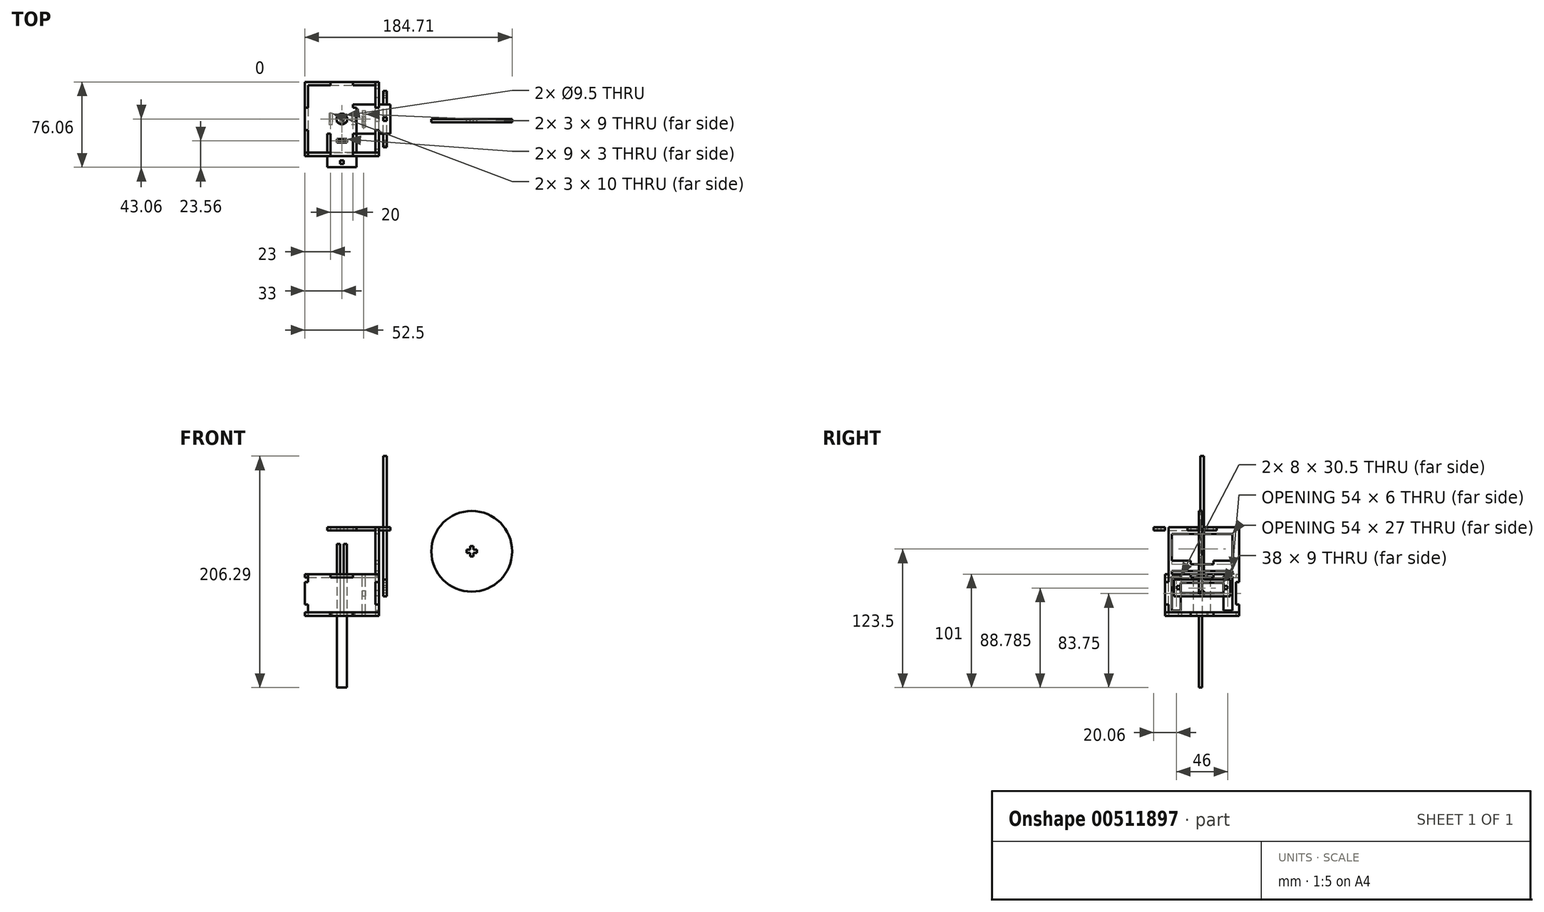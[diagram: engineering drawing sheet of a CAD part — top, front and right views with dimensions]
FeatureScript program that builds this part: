
annotation { "Feature Type Name" : "Feature", "Feature Type Description" : "" }
export const myFeature = defineFeature(function(context is Context, id is Id, definition is map)
    precondition{}
    {
        {
            var Q0;
            Q0=qCreatedBy(makeId("Top.planeOp"),FACE);
            var sketch = newSketch(context, id + "F0", { "sketchPlane" : qUnion([Q0])});
            skLineSegment(sketch, "E0.bottom", {"start": v(33, 33) * mm, "end": v(-33, 33) * mm});
            skLineSegment(sketch, "E0.top", {"start": v(33, -33) * mm, "end": v(-33, -33) * mm});
            skLineSegment(sketch, "E0.left", {"start": v(33, 33) * mm, "end": v(33, -33) * mm});
            skLineSegment(sketch, "E0.right", {"start": v(-33, 33) * mm, "end": v(-33, -33) * mm});
            skLineSegment(sketch, "E1.bottom", {"start": v(-10, 33) * mm, "end": v(10, 33) * mm});
            skLineSegment(sketch, "E1.top", {"start": v(-10, 30) * mm, "end": v(10, 30) * mm});
            skLineSegment(sketch, "E1.left", {"start": v(-10, 33) * mm, "end": v(-10, 30) * mm});
            skLineSegment(sketch, "E1.right", {"start": v(10, 33) * mm, "end": v(10, 30) * mm});
            skLineSegment(sketch, "E2.bottom", {"start": v(33, 10) * mm, "end": v(30, 10) * mm});
            skLineSegment(sketch, "E2.top", {"start": v(33, -10) * mm, "end": v(30, -10) * mm});
            skLineSegment(sketch, "E2.left", {"start": v(33, 10) * mm, "end": v(33, -10) * mm});
            skLineSegment(sketch, "E2.right", {"start": v(30, 10) * mm, "end": v(30, -10) * mm});
            skLineSegment(sketch, "E3.bottom", {"start": v(10, -33) * mm, "end": v(-10, -33) * mm});
            skLineSegment(sketch, "E3.top", {"start": v(10, -30) * mm, "end": v(-10, -30) * mm});
            skLineSegment(sketch, "E3.left", {"start": v(10, -33) * mm, "end": v(10, -30) * mm});
            skLineSegment(sketch, "E3.right", {"start": v(-10, -33) * mm, "end": v(-10, -30) * mm});
            skLineSegment(sketch, "E4.bottom", {"start": v(-33, 10) * mm, "end": v(-30, 10) * mm});
            skLineSegment(sketch, "E4.top", {"start": v(-33, -10) * mm, "end": v(-30, -10) * mm});
            skLineSegment(sketch, "E4.left", {"start": v(-33, 10) * mm, "end": v(-33, -10) * mm});
            skLineSegment(sketch, "E4.right", {"start": v(-30, 10) * mm, "end": v(-30, -10) * mm});
            skPoint(sketch, "E5", {"position": v(-30, 0) * mm});
            skPoint(sketch, "E6", {"position": v(0, 30) * mm});
            skPoint(sketch, "E7", {"position": v(0, -30) * mm});
            skPoint(sketch, "E8", {"position": v(30, 0) * mm});
            skCircle(sketch, "E9", {"center": v(0, 0) * mm, "radius": 4.75 * mm});
            skLineSegment(sketch, "E10.bottom", {"start": v(-8.5, 5) * mm, "end": v(-11.5, 5) * mm});
            skLineSegment(sketch, "E10.top", {"start": v(-8.5, -5) * mm, "end": v(-11.5, -5) * mm});
            skLineSegment(sketch, "E10.left", {"start": v(-8.5, 5) * mm, "end": v(-8.5, -5) * mm});
            skLineSegment(sketch, "E10.right", {"start": v(-11.5, 5) * mm, "end": v(-11.5, -5) * mm});
            skPoint(sketch, "E10.middle", {"position": v(-10, 0) * mm});
            skLineSegment(sketch, "E11.bottom", {"start": v(11.5, 5) * mm, "end": v(8.5, 5) * mm});
            skLineSegment(sketch, "E11.top", {"start": v(11.5, -5) * mm, "end": v(8.5, -5) * mm});
            skLineSegment(sketch, "E11.left", {"start": v(11.5, 5) * mm, "end": v(11.5, -5) * mm});
            skLineSegment(sketch, "E11.right", {"start": v(8.5, 5) * mm, "end": v(8.5, -5) * mm});
            skPoint(sketch, "E11.middle", {"position": v(10, 0) * mm});
            skLineSegment(sketch, "E12", {"start": v(33, 0) * mm, "end": v(-33, 0) * mm, "construction": true});
            skSolve(sketch);
        }
        {
            var Q0;
            Q0=makeQuery(id+"F0.imprint","IMPRINT",FACE,{"disambiguationData":[TD([[makeQuery(id+"F0.imprint","IMPRINT",EDGE,{"derivedFrom":sQuery(id+"F0.wireOp",EDGE,"E0.bottom")}),1.0]])]});
            extrude(context, id + "F1", {"entities" : qUnion([Q0]), "depth" : 3 * mm, "offsetDistance" : 25 * mm});
        }
        {
            var Q0;
            Q0=makeQuery(id+"F1.opExtrude","SWEPT_FACE",FACE,{"disambiguationData":[OSD([sQuery(id+"F0.wireOp",EDGE,"E2.right")])]});
            var sketch = newSketch(context, id + "F2", { "sketchPlane" : qUnion([Q0])});
            skLineSegment(sketch, "E13.bottom", {"start": v(-33, 3) * mm, "end": v(33, 3) * mm});
            skLineSegment(sketch, "E13.top", {"start": v(-33, 37) * mm, "end": v(33, 37) * mm});
            skLineSegment(sketch, "E13.left", {"start": v(-33, 3) * mm, "end": v(-33, 37) * mm});
            skLineSegment(sketch, "E13.right", {"start": v(33, 3) * mm, "end": v(33, 37) * mm});
            skLineSegment(sketch, "E14.bottom", {"start": v(-10, 3) * mm, "end": v(10, 3) * mm});
            skLineSegment(sketch, "E14.top", {"start": v(-10, 0) * mm, "end": v(10, 0) * mm});
            skLineSegment(sketch, "E14.left", {"start": v(-10, 3) * mm, "end": v(-10, 0) * mm});
            skLineSegment(sketch, "E14.right", {"start": v(10, 3) * mm, "end": v(10, 0) * mm});
            skCircle(sketch, "E15", {"center": v(0, 20) * mm, "radius": 2.3 * mm});
            skLineSegment(sketch, "E16.bottom", {"start": v(33, 30) * mm, "end": v(30, 30) * mm});
            skLineSegment(sketch, "E16.top", {"start": v(33, 10) * mm, "end": v(30, 10) * mm});
            skLineSegment(sketch, "E16.left", {"start": v(33, 30) * mm, "end": v(33, 10) * mm});
            skLineSegment(sketch, "E16.right", {"start": v(30, 30) * mm, "end": v(30, 10) * mm});
            skLineSegment(sketch, "E17.bottom", {"start": v(-33, 30) * mm, "end": v(-30, 30) * mm});
            skLineSegment(sketch, "E17.top", {"start": v(-33, 10) * mm, "end": v(-30, 10) * mm});
            skLineSegment(sketch, "E17.left", {"start": v(-33, 30) * mm, "end": v(-33, 10) * mm});
            skLineSegment(sketch, "E17.right", {"start": v(-30, 30) * mm, "end": v(-30, 10) * mm});
            skLineSegment(sketch, "E18.bottom", {"start": v(10, 37) * mm, "end": v(-10, 37) * mm});
            skLineSegment(sketch, "E18.top", {"start": v(10, 34) * mm, "end": v(-10, 34) * mm});
            skLineSegment(sketch, "E18.left", {"start": v(10, 37) * mm, "end": v(10, 34) * mm});
            skLineSegment(sketch, "E18.right", {"start": v(-10, 37) * mm, "end": v(-10, 34) * mm});
            skPoint(sketch, "E19", {"position": v(0, 34) * mm});
            skPoint(sketch, "E20", {"position": v(30, 20) * mm});
            skPoint(sketch, "E21", {"position": v(-30, 20) * mm});
            skLineSegment(sketch, "E22", {"start": v(-33, 37) * mm, "end": v(-33, 49) * mm});
            skLineSegment(sketch, "E23", {"start": v(-33, 49) * mm, "end": v(-10, 49) * mm});
            skLineSegment(sketch, "E24", {"start": v(-10, 49) * mm, "end": v(-10, 46) * mm});
            skLineSegment(sketch, "E25", {"start": v(-10, 46) * mm, "end": v(10, 46) * mm});
            skLineSegment(sketch, "E26", {"start": v(10, 46) * mm, "end": v(10, 49) * mm});
            skLineSegment(sketch, "E27", {"start": v(10, 49) * mm, "end": v(33, 49) * mm});
            skLineSegment(sketch, "E28", {"start": v(33, 49) * mm, "end": v(33, 37) * mm});
            skLineSegment(sketch, "E29", {"start": v(0, 20) * mm, "end": v(0, 46) * mm, "construction": true});
            skLineSegment(sketch, "E30", {"start": v(-27, 37) * mm, "end": v(-27, 40) * mm});
            skLineSegment(sketch, "E31", {"start": v(-27, 40) * mm, "end": v(27, 40) * mm});
            skLineSegment(sketch, "E32", {"start": v(27, 40) * mm, "end": v(27, 37) * mm});
            skPoint(sketch, "E33", {"position": v(0, 40) * mm});
            skLineSegment(sketch, "E34", {"start": v(-33, 49) * mm, "end": v(-33, 79) * mm});
            skLineSegment(sketch, "E35", {"start": v(-33, 79) * mm, "end": v(-10, 79) * mm});
            skLineSegment(sketch, "E36", {"start": v(-10, 79) * mm, "end": v(-10, 76) * mm});
            skLineSegment(sketch, "E37", {"start": v(-10, 76) * mm, "end": v(10, 76) * mm});
            skLineSegment(sketch, "E38", {"start": v(10, 76) * mm, "end": v(10, 79) * mm});
            skLineSegment(sketch, "E39", {"start": v(10, 79) * mm, "end": v(33, 79) * mm});
            skLineSegment(sketch, "E40", {"start": v(33, 79) * mm, "end": v(33, 49) * mm});
            skLineSegment(sketch, "E41", {"start": v(-27, 49) * mm, "end": v(-27, 73) * mm});
            skLineSegment(sketch, "E42", {"start": v(-27, 73) * mm, "end": v(27, 73) * mm});
            skLineSegment(sketch, "E43", {"start": v(27, 73) * mm, "end": v(27, 49) * mm});
            skPoint(sketch, "E44", {"position": v(0, 73) * mm});
            skLineSegment(sketch, "E45", {"start": v(0, 46) * mm, "end": v(0, 73) * mm, "construction": true});
            skLineSegment(sketch, "E46", {"start": v(-30, 30) * mm, "end": v(-30, 37) * mm});
            skLineSegment(sketch, "E47", {"start": v(-30, 10) * mm, "end": v(-30, 3) * mm});
            skLineSegment(sketch, "E48", {"start": v(-30, 37) * mm, "end": v(-30, 79) * mm});
            skLineSegment(sketch, "E49.bottom", {"start": v(-27, 37) * mm, "end": v(-24, 37) * mm});
            skLineSegment(sketch, "E50.bottom", {"start": v(27, 37) * mm, "end": v(24, 37) * mm});
            skLineSegment(sketch, "E51.bottom", {"start": v(27, 3) * mm, "end": v(24, 3) * mm});
            skLineSegment(sketch, "E52.bottom", {"start": v(-27, 35) * mm, "end": v(-19, 35) * mm});
            skLineSegment(sketch, "E52.top", {"start": v(-27, 4.5) * mm, "end": v(-19, 4.5) * mm});
            skLineSegment(sketch, "E52.left", {"start": v(-27, 35) * mm, "end": v(-27, 4.5) * mm});
            skLineSegment(sketch, "E52.right", {"start": v(-19, 35) * mm, "end": v(-19, 4.5) * mm});
            skLineSegment(sketch, "E53.bottom", {"start": v(27, 35) * mm, "end": v(19, 35) * mm});
            skLineSegment(sketch, "E53.top", {"start": v(27, 4.5) * mm, "end": v(19, 4.5) * mm});
            skLineSegment(sketch, "E53.left", {"start": v(27, 35) * mm, "end": v(27, 4.5) * mm});
            skLineSegment(sketch, "E53.right", {"start": v(19, 35) * mm, "end": v(19, 4.5) * mm});
            skSolve(sketch);
        }
        {
            var Q0;
            Q0=makeQuery(id+"F2.imprint","IMPRINT",FACE,{"disambiguationData":[TD([[makeQuery(id+"F2.imprint","IMPRINT",EDGE,{"derivedFrom":sQuery(id+"F2.wireOp",EDGE,"E13.top")}),-1.0]])]});
            var Q1;
            Q1=makeQuery(id+"F2.imprint","IMPRINT",FACE,{"disambiguationData":[TD([[makeQuery(id+"F2.imprint","IMPRINT",EDGE,{"derivedFrom":sQuery(id+"F2.wireOp",EDGE,"E14.bottom")}),1.0]])]});
            var Q2;
            Q2=makeQuery(id+"F2.imprint","IMPRINT",FACE,{"disambiguationData":[TD([[makeQuery(id+"F2.imprint","IMPRINT",EDGE,{"derivedFrom":sQuery(id+"F2.wireOp",EDGE,"E17.bottom")}),-1.0]])]});
            var Q3;
            {var subQ7=sQuery(id+"F2.wireOp",EDGE,"E36");Q3=makeQuery(id+"F2.imprint","IMPRINT",FACE,{"disambiguationData":[TD([[makeQuery(id+"F2.imprint","IMPRINT",EDGE,{"derivedFrom":subQ7}),-1.0]])]});}
            var Q4;
            {var subQ4=sQuery(id+"F2.wireOp",EDGE,"E24");Q4=makeQuery(id+"F2.imprint","IMPRINT",FACE,{"disambiguationData":[TD([[makeQuery(id+"F2.imprint","IMPRINT",EDGE,{"derivedFrom":subQ4}),-1.0]])]});}
            extrude(context, id + "F3", {"entities" : qUnion([Q0, Q1, Q2, Q3, Q4]), "depth" : 3 * mm, "offsetDistance" : 25 * mm});
        }
        {
            var Q0;
            Q0=qCreatedBy(makeId("Front.planeOp"),FACE);
            var sketch = newSketch(context, id + "F4", { "sketchPlane" : qUnion([Q0])});
            skLineSegment(sketch, "E54.bottom", {"start": v(4.5, 64) * mm, "end": v(-4.5, 64) * mm});
            skLineSegment(sketch, "E54.top", {"start": v(4.5, -64) * mm, "end": v(-4.5, -64) * mm});
            skLineSegment(sketch, "E54.left", {"start": v(4.5, 64) * mm, "end": v(4.5, -64) * mm});
            skLineSegment(sketch, "E54.right", {"start": v(-4.5, 64) * mm, "end": v(-4.5, -64) * mm});
            skPoint(sketch, "E54.middle", {"position": v(0, 0) * mm});
            skLineSegment(sketch, "E55.bottom", {"start": v(-1.5, 64) * mm, "end": v(1.5, 64) * mm});
            skLineSegment(sketch, "E55.top", {"start": v(-1.5, 0) * mm, "end": v(1.5, 0) * mm});
            skLineSegment(sketch, "E55.left", {"start": v(-1.5, 64) * mm, "end": v(-1.5, 0) * mm});
            skLineSegment(sketch, "E55.right", {"start": v(1.5, 64) * mm, "end": v(1.5, 0) * mm});
            skSolve(sketch);
        }
        {
            var Q0;
            Q0=makeQuery(id+"F4.imprint","IMPRINT",FACE,{"disambiguationData":[TD([[makeQuery(id+"F4.imprint","IMPRINT",EDGE,{"derivedFrom":sQuery(id+"F4.wireOp",EDGE,"E54.top")}),-1.0]])]});
            extrude(context, id + "F5", {"entities" : qUnion([Q0]), "depth" : 3 * mm, "offsetDistance" : 25 * mm});
        }
        {
            var Q0;
            Q0=makeQuery(id+"F3.opExtrude","SWEPT_FACE",FACE,{"disambiguationData":[OSD([sQuery(id+"F2.wireOp",EDGE,"E18.top")])]});
            var sketch = newSketch(context, id + "F6", { "sketchPlane" : qUnion([Q0])});
            skLineSegment(sketch, "E56.bottom", {"start": v(-30, -30) * mm, "end": v(30, -30) * mm});
            skLineSegment(sketch, "E56.top", {"start": v(-30, 30) * mm, "end": v(30, 30) * mm});
            skLineSegment(sketch, "E56.left", {"start": v(-30, -30) * mm, "end": v(-30, 30) * mm});
            skLineSegment(sketch, "E56.right", {"start": v(30, -30) * mm, "end": v(30, 30) * mm});
            skLineSegment(sketch, "E57.bottom", {"start": v(10, 30) * mm, "end": v(-10, 30) * mm});
            skLineSegment(sketch, "E57.top", {"start": v(10, 33) * mm, "end": v(-10, 33) * mm});
            skLineSegment(sketch, "E57.left", {"start": v(10, 30) * mm, "end": v(10, 33) * mm});
            skLineSegment(sketch, "E57.right", {"start": v(-10, 30) * mm, "end": v(-10, 33) * mm});
            skLineSegment(sketch, "E58.bottom", {"start": v(10, -30) * mm, "end": v(-10, -30) * mm});
            skLineSegment(sketch, "E58.top", {"start": v(10, -33) * mm, "end": v(-10, -33) * mm});
            skLineSegment(sketch, "E58.left", {"start": v(10, -30) * mm, "end": v(10, -33) * mm});
            skLineSegment(sketch, "E58.right", {"start": v(-10, -30) * mm, "end": v(-10, -33) * mm});
            skLineSegment(sketch, "E59.bottom", {"start": v(30, -10) * mm, "end": v(33, -10) * mm});
            skLineSegment(sketch, "E59.top", {"start": v(30, 10) * mm, "end": v(33, 10) * mm});
            skLineSegment(sketch, "E59.left", {"start": v(30, -10) * mm, "end": v(30, 10) * mm});
            skLineSegment(sketch, "E59.right", {"start": v(33, -10) * mm, "end": v(33, 10) * mm});
            skLineSegment(sketch, "E60.bottom", {"start": v(-30, 10) * mm, "end": v(-33, 10) * mm});
            skLineSegment(sketch, "E60.top", {"start": v(-30, -10) * mm, "end": v(-33, -10) * mm});
            skLineSegment(sketch, "E60.left", {"start": v(-30, 10) * mm, "end": v(-30, -10) * mm});
            skLineSegment(sketch, "E60.right", {"start": v(-33, 10) * mm, "end": v(-33, -10) * mm});
            skCircle(sketch, "E61", {"center": v(0, 0) * mm, "radius": 4.75 * mm});
            skSolve(sketch);
        }
        {
            var Q0;
            Q0 = qSketchRegion(id + "F6", true);
            extrude(context, id + "F7", {"entities" : qUnion([Q0]), "depth" : 3 * mm, "offsetDistance" : 25 * mm});
        }
        {
            var Q0;
            {var subQ0=sQuery(id+"F6.wireOp",EDGE,"E56.bottom");Q0=makeQuery(id+"F7.opExtrude","SWEPT_FACE",FACE,{"disambiguationData":[OSD([subQ0]),TDD([makeQuery(id+"F6.imprint","IMPRINT",EDGE,{"disambiguationData":[TD([[makeQuery(id+"F6.imprint","INTERSECT",VERTEX,{"derivedFrom":[subQ0,sQuery(id+"F6.wireOp",EDGE,"E56.right")]}),1.0]])],"derivedFrom":subQ0})])]});}
            var sketch = newSketch(context, id + "F8", { "sketchPlane" : qUnion([Q0])});
            skLineSegment(sketch, "E62.bottom", {"start": v(-30, 3) * mm, "end": v(30, 3) * mm});
            skLineSegment(sketch, "E62.top", {"start": v(-30, 37) * mm, "end": v(30, 37) * mm});
            skLineSegment(sketch, "E62.left", {"start": v(-30, 3) * mm, "end": v(-30, 37) * mm});
            skLineSegment(sketch, "E62.right", {"start": v(30, 3) * mm, "end": v(30, 37) * mm});
            skLineSegment(sketch, "E63.bottom", {"start": v(10, 37) * mm, "end": v(-10, 37) * mm});
            skLineSegment(sketch, "E63.top", {"start": v(10, 34) * mm, "end": v(-10, 34) * mm});
            skLineSegment(sketch, "E63.left", {"start": v(10, 34) * mm, "end": v(10, 37) * mm});
            skLineSegment(sketch, "E63.right", {"start": v(-10, 34) * mm, "end": v(-10, 37) * mm});
            skLineSegment(sketch, "E64.bottom", {"start": v(-30, 30) * mm, "end": v(-33, 30) * mm});
            skLineSegment(sketch, "E64.top", {"start": v(-30, 10) * mm, "end": v(-33, 10) * mm});
            skLineSegment(sketch, "E64.left", {"start": v(-30, 30) * mm, "end": v(-30, 10) * mm});
            skLineSegment(sketch, "E64.right", {"start": v(-33, 30) * mm, "end": v(-33, 10) * mm});
            skLineSegment(sketch, "E65.bottom", {"start": v(-10, 3) * mm, "end": v(10, 3) * mm});
            skLineSegment(sketch, "E65.top", {"start": v(-10, 0) * mm, "end": v(10, 0) * mm});
            skLineSegment(sketch, "E65.left", {"start": v(-10, 3) * mm, "end": v(-10, 0) * mm});
            skLineSegment(sketch, "E65.right", {"start": v(10, 3) * mm, "end": v(10, 0) * mm});
            skLineSegment(sketch, "E66.bottom", {"start": v(30, 10) * mm, "end": v(33, 10) * mm});
            skLineSegment(sketch, "E66.top", {"start": v(30, 30) * mm, "end": v(33, 30) * mm});
            skLineSegment(sketch, "E66.left", {"start": v(30, 10) * mm, "end": v(30, 30) * mm});
            skLineSegment(sketch, "E66.right", {"start": v(33, 10) * mm, "end": v(33, 30) * mm});
            skLineSegment(sketch, "E67.0", {"start": v(33, 37) * mm, "end": v(30, 37) * mm});
            skLineSegment(sketch, "E68.0", {"start": v(33, 30) * mm, "end": v(33, 37) * mm});
            skLineSegment(sketch, "E69.0", {"start": v(33, 10) * mm, "end": v(33, 3) * mm});
            skLineSegment(sketch, "E70.0", {"start": v(33, 3) * mm, "end": v(30, 3) * mm});
            skSolve(sketch);
        }
        {
            var Q0;
            Q0=makeQuery(id+"F8.imprint","IMPRINT",FACE,{"disambiguationData":[TD([[makeQuery(id+"F8.imprint","IMPRINT",EDGE,{"derivedFrom":sQuery(id+"F8.wireOp",EDGE,"E63.top")}),1.0]])]});
            var Q1;
            Q1=makeQuery(id+"F8.imprint","IMPRINT",FACE,{"disambiguationData":[TD([[makeQuery(id+"F8.imprint","IMPRINT",EDGE,{"derivedFrom":sQuery(id+"F8.wireOp",EDGE,"E64.bottom")}),1.0]])]});
            var Q2;
            Q2=makeQuery(id+"F8.imprint","IMPRINT",FACE,{"disambiguationData":[TD([[makeQuery(id+"F8.imprint","IMPRINT",EDGE,{"derivedFrom":sQuery(id+"F8.wireOp",EDGE,"E65.bottom")}),-1.0]])]});
            var Q3;
            Q3=makeQuery(id+"F8.imprint","IMPRINT",FACE,{"disambiguationData":[TD([[makeQuery(id+"F8.imprint","IMPRINT",EDGE,{"derivedFrom":sQuery(id+"F8.wireOp",EDGE,"E66.bottom")}),-1.0]])]});
            var Q4;
            {var subQ3=sQuery(id+"F8.wireOp",EDGE,"E63.left");Q4=makeQuery(id+"F8.imprint","IMPRINT",FACE,{"disambiguationData":[TD([[makeQuery(id+"F8.imprint","IMPRINT",EDGE,{"derivedFrom":subQ3}),1.0]])]});}
            var Q5;
            {var subQ4=sQuery(id+"F8.wireOp",EDGE,"E66.top");Q5=makeQuery(id+"F8.imprint","IMPRINT",FACE,{"disambiguationData":[TD([[makeQuery(id+"F8.imprint","IMPRINT",EDGE,{"derivedFrom":subQ4}),1.0]])]});}
            extrude(context, id + "F9", {"entities" : qUnion([Q0, Q1, Q2, Q3, Q4, Q5]), "depth" : 3 * mm, "offsetDistance" : 25 * mm});
        }
        {
            var Q0;
            Q0=makeQuery(id+"F3.opExtrude","SWEPT_FACE",FACE,{"disambiguationData":[OSD([sQuery(id+"F2.wireOp",EDGE,"E37")])]});
            var sketch = newSketch(context, id + "F10", { "sketchPlane" : qUnion([Q0])});
            skLineSegment(sketch, "E71.bottom", {"start": v(0, 10) * mm, "end": v(33, 10) * mm});
            skLineSegment(sketch, "E71.top", {"start": v(0, -10) * mm, "end": v(33, -10) * mm});
            skLineSegment(sketch, "E71.left", {"start": v(0, 10) * mm, "end": v(0, -10) * mm});
            skLineSegment(sketch, "E71.right", {"start": v(33, 10) * mm, "end": v(33, -10) * mm});
            skLineSegment(sketch, "E72.bottom", {"start": v(33, -13) * mm, "end": v(43.06, -13) * mm});
            skLineSegment(sketch, "E72.top", {"start": v(33, 13) * mm, "end": v(43.06, 13) * mm});
            skLineSegment(sketch, "E72.left", {"start": v(33, -13) * mm, "end": v(33, 13) * mm});
            skLineSegment(sketch, "E72.right", {"start": v(43.06, -13) * mm, "end": v(43.06, 13) * mm});
            skLineSegment(sketch, "E73", {"start": v(38.5, 13) * mm, "end": v(38.5, -13) * mm, "construction": true});
            skLineSegment(sketch, "E74.MirrorCS", {"start": v(-33, 10) * mm, "end": v(-33, -10) * mm});
            skLineSegment(sketch, "E75.MirrorCS", {"start": v(-33, -13) * mm, "end": v(-43.06, -13) * mm});
            skLineSegment(sketch, "E76.MirrorCS", {"start": v(-33, -13) * mm, "end": v(-33, 13) * mm});
            skLineSegment(sketch, "E77.MirrorCS", {"start": v(-43.06, -13) * mm, "end": v(-43.06, 13) * mm});
            skLineSegment(sketch, "E78.MirrorCS", {"start": v(-38.5, 13) * mm, "end": v(-38.5, -13) * mm, "construction": true});
            skLineSegment(sketch, "E79.MirrorCS", {"start": v(-33, 13) * mm, "end": v(-43.06, 13) * mm});
            skLineSegment(sketch, "E80.MirrorCS", {"start": v(0, -10) * mm, "end": v(-33, -10) * mm});
            skLineSegment(sketch, "E81.MirrorCS", {"start": v(0, 10) * mm, "end": v(-33, 10) * mm});
            skCircle(sketch, "E82", {"center": v(0, 0) * mm, "radius": 4.75 * mm});
            skLineSegment(sketch, "E83.bottom", {"start": v(40.06, 1.56) * mm, "end": v(36.94, 1.56) * mm});
            skLineSegment(sketch, "E83.top", {"start": v(40.06, -1.56) * mm, "end": v(36.94, -1.56) * mm});
            skLineSegment(sketch, "E83.left", {"start": v(40.06, 1.56) * mm, "end": v(40.06, -1.56) * mm});
            skLineSegment(sketch, "E83.right", {"start": v(36.94, 1.56) * mm, "end": v(36.94, -1.56) * mm});
            skPoint(sketch, "E83.middle", {"position": v(38.5, 0) * mm});
            skLineSegment(sketch, "E84.bottom", {"start": v(-36.94, 1.56) * mm, "end": v(-40.06, 1.56) * mm});
            skLineSegment(sketch, "E84.top", {"start": v(-36.94, -1.56) * mm, "end": v(-40.06, -1.56) * mm});
            skLineSegment(sketch, "E84.left", {"start": v(-36.94, 1.56) * mm, "end": v(-36.94, -1.56) * mm});
            skLineSegment(sketch, "E84.right", {"start": v(-40.06, 1.56) * mm, "end": v(-40.06, -1.56) * mm});
            skPoint(sketch, "E84.middle", {"position": v(-38.5, 0) * mm});
            skLineSegment(sketch, "E85.bottom", {"start": v(30, 10) * mm, "end": v(-30, 10) * mm});
            skLineSegment(sketch, "E85.top", {"start": v(30, 13) * mm, "end": v(-30, 13) * mm});
            skLineSegment(sketch, "E85.left", {"start": v(30, 10) * mm, "end": v(30, 13) * mm});
            skLineSegment(sketch, "E85.right", {"start": v(-30, 10) * mm, "end": v(-30, 13) * mm});
            skLineSegment(sketch, "E86.bottom", {"start": v(-30, -10) * mm, "end": v(30, -10) * mm});
            skLineSegment(sketch, "E86.top", {"start": v(-30, -13) * mm, "end": v(30, -13) * mm});
            skLineSegment(sketch, "E86.left", {"start": v(-30, -10) * mm, "end": v(-30, -13) * mm});
            skLineSegment(sketch, "E86.right", {"start": v(30, -10) * mm, "end": v(30, -13) * mm});
            skLineSegment(sketch, "E87.1.0", {"start": v(10, 0) * mm, "end": v(10, 33) * mm});
            skLineSegment(sketch, "E87.1.1", {"start": v(-13, 33) * mm, "end": v(13, 33) * mm});
            skLineSegment(sketch, "E87.1.2", {"start": v(13, -30) * mm, "end": v(13, 30) * mm});
            skLineSegment(sketch, "E87.1.3", {"start": v(10, -30) * mm, "end": v(10, 30) * mm});
            skLineSegment(sketch, "E87.1.4", {"start": v(13, 33) * mm, "end": v(13, 43.06) * mm});
            skPoint(sketch, "E87.1.5", {"position": v(0, -38.5) * mm});
            skLineSegment(sketch, "E87.1.6", {"start": v(-13, 43.06) * mm, "end": v(13, 43.06) * mm});
            skLineSegment(sketch, "E87.1.7", {"start": v(13, 38.5) * mm, "end": v(-13, 38.5) * mm, "construction": true});
            skLineSegment(sketch, "E87.1.8", {"start": v(-13, -43.06) * mm, "end": v(13, -43.06) * mm});
            skLineSegment(sketch, "E87.1.9", {"start": v(13, -38.5) * mm, "end": v(-13, -38.5) * mm, "construction": true});
            skPoint(sketch, "E87.1.10", {"position": v(0, 38.5) * mm});
            skLineSegment(sketch, "E87.1.11", {"start": v(13, -33) * mm, "end": v(13, -43.06) * mm});
            skLineSegment(sketch, "E87.1.13", {"start": v(-13, -33) * mm, "end": v(-13, -43.06) * mm});
            skLineSegment(sketch, "E87.1.14", {"start": v(-13, 30) * mm, "end": v(-13, -30) * mm});
            skLineSegment(sketch, "E87.1.15", {"start": v(10, 0) * mm, "end": v(-10, 0) * mm});
            skLineSegment(sketch, "E87.1.16", {"start": v(-13, -33) * mm, "end": v(13, -33) * mm});
            skLineSegment(sketch, "E87.1.17", {"start": v(-10, 30) * mm, "end": v(-10, -30) * mm});
            skLineSegment(sketch, "E87.1.18", {"start": v(-13, 33) * mm, "end": v(-13, 43.06) * mm});
            skLineSegment(sketch, "E87.1.19", {"start": v(10, -33) * mm, "end": v(-10, -33) * mm});
            skLineSegment(sketch, "E87.1.20", {"start": v(-10, 0) * mm, "end": v(-10, 33) * mm});
            skLineSegment(sketch, "E87.1.21", {"start": v(10, 0) * mm, "end": v(10, -33) * mm});
            skLineSegment(sketch, "E87.1.22", {"start": v(-10, 0) * mm, "end": v(-10, -33) * mm});
            skLineSegment(sketch, "E87.1.23", {"start": v(10, 33) * mm, "end": v(-10, 33) * mm});
            skLineSegment(sketch, "E87.1.24", {"start": v(1.56, -40.06) * mm, "end": v(1.56, -36.94) * mm});
            skLineSegment(sketch, "E87.1.25", {"start": v(-1.56, -40.06) * mm, "end": v(-1.56, -36.94) * mm});
            skLineSegment(sketch, "E87.1.26", {"start": v(1.56, 36.94) * mm, "end": v(-1.56, 36.94) * mm});
            skLineSegment(sketch, "E87.1.27", {"start": v(-1.56, 36.94) * mm, "end": v(-1.56, 40.06) * mm});
            skLineSegment(sketch, "E87.1.28", {"start": v(1.56, 40.06) * mm, "end": v(-1.56, 40.06) * mm});
            skLineSegment(sketch, "E87.1.29", {"start": v(-10, -30) * mm, "end": v(-13, -30) * mm});
            skLineSegment(sketch, "E87.1.30", {"start": v(-10, 30) * mm, "end": v(-13, 30) * mm});
            skLineSegment(sketch, "E87.1.31", {"start": v(10, -30) * mm, "end": v(13, -30) * mm});
            skLineSegment(sketch, "E87.1.32", {"start": v(1.56, 36.94) * mm, "end": v(1.56, 40.06) * mm});
            skLineSegment(sketch, "E87.1.33", {"start": v(1.56, -36.94) * mm, "end": v(-1.56, -36.94) * mm});
            skLineSegment(sketch, "E87.1.34", {"start": v(10, 30) * mm, "end": v(13, 30) * mm});
            skLineSegment(sketch, "E87.1.35", {"start": v(1.56, -40.06) * mm, "end": v(-1.56, -40.06) * mm});
            skLineSegment(sketch, "E87.anchor1", {"start": v(0, 0) * mm, "end": v(-43.06, -13) * mm, "construction": true});
            skLineSegment(sketch, "E87.anchor2", {"start": v(0, 0) * mm, "end": v(-13, 43.06) * mm, "construction": true});
            skSolve(sketch);
        }
        {
            var Q0;
            {var subQ0=sQuery(id+"F10.wireOp",EDGE,"E85.left");Q0=makeQuery(id+"F10.imprint","IMPRINT",FACE,{"disambiguationData":[TD([[makeQuery(id+"F10.imprint","IMPRINT",EDGE,{"derivedFrom":subQ0}),1.0]])]});}
            var Q1;
            {var subQ0=sQuery(id+"F10.wireOp",EDGE,"E87.1.2");var subQ1=sQuery(id+"F10.wireOp",EDGE,"E85.bottom");var subQ2=makeQuery(id+"F10.imprint","INTERSECT",VERTEX,{"derivedFrom":[subQ1,subQ0]});Q1=makeQuery(id+"F10.imprint","IMPRINT",FACE,{"disambiguationData":[TD([[makeQuery(id+"F10.imprint","IMPRINT",EDGE,{"disambiguationData":[TD([[subQ2,-1.0]])],"derivedFrom":subQ1}),-1.0]])]});}
            var Q2;
            {var subQ0=sQuery(id+"F10.wireOp",EDGE,"E87.1.20");var subQ1=sQuery(id+"F10.wireOp",EDGE,"E85.bottom");var subQ2=makeQuery(id+"F10.imprint","INTERSECT",VERTEX,{"derivedFrom":[subQ1,subQ0]});Q2=makeQuery(id+"F10.imprint","IMPRINT",FACE,{"disambiguationData":[TD([[makeQuery(id+"F10.imprint","IMPRINT",EDGE,{"disambiguationData":[TD([[subQ2,-1.0]])],"derivedFrom":subQ1}),-1.0]])]});}
            var Q3;
            {var subQ4=sQuery(id+"F10.wireOp",EDGE,"E72.bottom");Q3=makeQuery(id+"F10.imprint","IMPRINT",FACE,{"disambiguationData":[TD([[makeQuery(id+"F10.imprint","IMPRINT",EDGE,{"derivedFrom":subQ4}),1.0]])]});}
            var Q4;
            {var subQ0=sQuery(id+"F10.wireOp",EDGE,"E71.bottom");Q4=makeQuery(id+"F10.imprint","IMPRINT",FACE,{"disambiguationData":[TD([[makeQuery(id+"F10.imprint","IMPRINT",EDGE,{"derivedFrom":subQ0}),1.0]])]});}
            var Q5;
            {var subQ0=sQuery(id+"F10.wireOp",EDGE,"E86.right");Q5=makeQuery(id+"F10.imprint","IMPRINT",FACE,{"disambiguationData":[TD([[makeQuery(id+"F10.imprint","IMPRINT",EDGE,{"derivedFrom":subQ0}),-1.0]])]});}
            var Q6;
            {var subQ0=sQuery(id+"F10.wireOp",EDGE,"E87.1.14");var subQ1=sQuery(id+"F10.wireOp",EDGE,"E86.bottom");var subQ2=makeQuery(id+"F10.imprint","INTERSECT",VERTEX,{"derivedFrom":[subQ1,subQ0]});Q6=makeQuery(id+"F10.imprint","IMPRINT",FACE,{"disambiguationData":[TD([[makeQuery(id+"F10.imprint","IMPRINT",EDGE,{"disambiguationData":[TD([[subQ2,-1.0]])],"derivedFrom":subQ1}),-1.0]])]});}
            var Q7;
            {var subQ0=sQuery(id+"F10.wireOp",EDGE,"E87.1.21");var subQ1=sQuery(id+"F10.wireOp",EDGE,"E86.bottom");var subQ2=makeQuery(id+"F10.imprint","INTERSECT",VERTEX,{"derivedFrom":[subQ1,subQ0]});Q7=makeQuery(id+"F10.imprint","IMPRINT",FACE,{"disambiguationData":[TD([[makeQuery(id+"F10.imprint","IMPRINT",EDGE,{"disambiguationData":[TD([[subQ2,-1.0]])],"derivedFrom":subQ1}),-1.0]])]});}
            var Q8;
            {var subQ1=sQuery(id+"F10.wireOp",EDGE,"E85.bottom");var subQ5=makeQuery(id+"F10.imprint","INTERSECT",VERTEX,{"derivedFrom":[sQuery(id+"F10.wireOp",EDGE,"E71.left"),subQ1]});Q8=makeQuery(id+"F10.imprint","IMPRINT",FACE,{"disambiguationData":[TD([[makeQuery(id+"F10.imprint","IMPRINT",EDGE,{"disambiguationData":[TD([[subQ5,1.0]])],"derivedFrom":subQ1}),-1.0]])]});}
            var Q9;
            {var subQ1=sQuery(id+"F10.wireOp",EDGE,"E85.bottom");var subQ6=sQuery(id+"F10.wireOp",EDGE,"E87.1.20");var subQ8=makeQuery(id+"F10.imprint","INTERSECT",VERTEX,{"derivedFrom":[subQ1,subQ6]});Q9=makeQuery(id+"F10.imprint","IMPRINT",FACE,{"disambiguationData":[TD([[makeQuery(id+"F10.imprint","IMPRINT",EDGE,{"disambiguationData":[TD([[subQ8,-1.0]])],"derivedFrom":subQ1}),1.0]])]});}
            var Q10;
            {var subQ1=sQuery(id+"F10.wireOp",EDGE,"E86.bottom");var subQ7=makeQuery(id+"F10.imprint","INTERSECT",VERTEX,{"derivedFrom":[sQuery(id+"F10.wireOp",EDGE,"E71.left"),subQ1]});Q10=makeQuery(id+"F10.imprint","IMPRINT",FACE,{"disambiguationData":[TD([[makeQuery(id+"F10.imprint","IMPRINT",EDGE,{"disambiguationData":[TD([[subQ7,1.0]])],"derivedFrom":subQ1}),-1.0]])]});}
            var Q11;
            {var subQ5=sQuery(id+"F10.wireOp",EDGE,"E71.left");var subQ7=sQuery(id+"F10.wireOp",EDGE,"E86.bottom");var subQ9=makeQuery(id+"F10.imprint","INTERSECT",VERTEX,{"derivedFrom":[subQ5,subQ7]});Q11=makeQuery(id+"F10.imprint","IMPRINT",FACE,{"disambiguationData":[TD([[makeQuery(id+"F10.imprint","IMPRINT",EDGE,{"disambiguationData":[TD([[subQ9,1.0]])],"derivedFrom":subQ5}),1.0]])]});}
            var Q12;
            {var subQ1=sQuery(id+"F10.wireOp",EDGE,"E71.left");var subQ5=sQuery(id+"F10.wireOp",EDGE,"E85.bottom");var subQ6=makeQuery(id+"F10.imprint","INTERSECT",VERTEX,{"derivedFrom":[subQ1,subQ5]});Q12=makeQuery(id+"F10.imprint","IMPRINT",FACE,{"disambiguationData":[TD([[makeQuery(id+"F10.imprint","IMPRINT",EDGE,{"disambiguationData":[TD([[subQ6,-1.0]])],"derivedFrom":subQ1}),1.0]])]});}
            var Q13;
            {var subQ1=sQuery(id+"F10.wireOp",EDGE,"E71.left");var subQ7=sQuery(id+"F10.wireOp",EDGE,"E85.bottom");var subQ8=makeQuery(id+"F10.imprint","INTERSECT",VERTEX,{"derivedFrom":[subQ1,subQ7]});Q13=makeQuery(id+"F10.imprint","IMPRINT",FACE,{"disambiguationData":[TD([[makeQuery(id+"F10.imprint","IMPRINT",EDGE,{"disambiguationData":[TD([[subQ8,-1.0]])],"derivedFrom":subQ1}),-1.0]])]});}
            var Q14;
            {var subQ5=sQuery(id+"F10.wireOp",EDGE,"E86.bottom");var subQ6=sQuery(id+"F10.wireOp",EDGE,"E71.left");var subQ7=makeQuery(id+"F10.imprint","INTERSECT",VERTEX,{"derivedFrom":[subQ6,subQ5]});Q14=makeQuery(id+"F10.imprint","IMPRINT",FACE,{"disambiguationData":[TD([[makeQuery(id+"F10.imprint","IMPRINT",EDGE,{"disambiguationData":[TD([[subQ7,1.0]])],"derivedFrom":subQ6}),-1.0]])]});}
            var Q15;
            {var subQ1=makeQuery(id+"F3.opExtrude","CAP_EDGE",EDGE,{"disambiguationData":[OSD([sQuery(id+"F2.wireOp",EDGE,"E37")])],"isStart":true});Q15=makeQuery(id+"F10.imprint","IMPRINT",FACE,{"disambiguationData":[TD([[makeQuery(id+"F10.imprint","IMPRINT",EDGE,{"derivedFrom":subQ1}),1.0]])]});}
            var Q16;
            {var subQ1=makeQuery(id+"F3.opExtrude","CAP_EDGE",EDGE,{"disambiguationData":[OSD([sQuery(id+"F2.wireOp",EDGE,"E37")])],"isStart":true});Q16=makeQuery(id+"F10.imprint","IMPRINT",FACE,{"disambiguationData":[TD([[makeQuery(id+"F10.imprint","IMPRINT",EDGE,{"derivedFrom":subQ1}),1.0]])]});}
            var Q17;
            {var subQ3=sQuery(id+"F10.wireOp",EDGE,"E85.bottom");var subQ5=sQuery(id+"F10.wireOp",EDGE,"E87.1.2");var subQ6=makeQuery(id+"F10.imprint","INTERSECT",VERTEX,{"derivedFrom":[subQ3,subQ5]});Q17=makeQuery(id+"F10.imprint","IMPRINT",FACE,{"disambiguationData":[TD([[makeQuery(id+"F10.imprint","IMPRINT",EDGE,{"disambiguationData":[TD([[subQ6,-1.0]])],"derivedFrom":subQ3}),1.0]])]});}
            var Q18;
            {var subQ5=sQuery(id+"F10.wireOp",EDGE,"E87.1.31");Q18=makeQuery(id+"F10.imprint","IMPRINT",FACE,{"disambiguationData":[TD([[makeQuery(id+"F10.imprint","IMPRINT",EDGE,{"derivedFrom":subQ5}),1.0]])]});}
            var Q19;
            {var subQ5=sQuery(id+"F10.wireOp",EDGE,"E87.1.29");Q19=makeQuery(id+"F10.imprint","IMPRINT",FACE,{"disambiguationData":[TD([[makeQuery(id+"F10.imprint","IMPRINT",EDGE,{"derivedFrom":subQ5}),-1.0]])]});}
            var Q20;
            {var subQ6=sQuery(id+"F10.wireOp",EDGE,"E87.1.19");Q20=makeQuery(id+"F10.imprint","IMPRINT",FACE,{"disambiguationData":[TD([[makeQuery(id+"F10.imprint","IMPRINT",EDGE,{"derivedFrom":subQ6}),-1.0]])]});}
            var Q21;
            Q21=makeQuery(id+"F10.imprint","IMPRINT",FACE,{"disambiguationData":[TD([[makeQuery(id+"F10.imprint","IMPRINT",EDGE,{"derivedFrom":sQuery(id+"F10.wireOp",EDGE,"E87.1.8")}),1.0]])]});
            extrude(context, id + "F11", {"entities" : qUnion([Q0, Q1, Q2, Q3, Q4, Q5, Q6, Q7, Q8, Q9, Q10, Q11, Q12, Q13, Q14, Q15, Q16, Q17, Q18, Q19, Q20, Q21]), "depth" : 3 * mm, "offsetDistance" : 25 * mm});
        }
        {
            var Q0;
            Q0=makeQuery(id+"F11.opExtrude","SWEPT_FACE",FACE,{"disambiguationData":[OSD([sQuery(id+"F10.wireOp",EDGE,"E83.right")])]});
            var sketch = newSketch(context, id + "F12", { "sketchPlane" : qUnion([Q0])});
            skLineSegment(sketch, "E88.bottom", {"start": v(-1.56, 32.29) * mm, "end": v(1.56, 32.29) * mm});
            skLineSegment(sketch, "E88.top", {"start": v(-1.56, 142.29) * mm, "end": v(1.56, 142.29) * mm});
            skLineSegment(sketch, "E88.left", {"start": v(-1.56, 32.29) * mm, "end": v(-1.56, 142.29) * mm});
            skLineSegment(sketch, "E88.right", {"start": v(1.56, 32.29) * mm, "end": v(1.56, 142.29) * mm});
            skLineSegment(sketch, "E89.bottom", {"start": v(-25, 32.29) * mm, "end": v(25, 32.29) * mm});
            skLineSegment(sketch, "E89.top", {"start": v(-25, 29.29) * mm, "end": v(25, 29.29) * mm});
            skLineSegment(sketch, "E89.left", {"start": v(-25, 32.29) * mm, "end": v(-25, 29.29) * mm});
            skLineSegment(sketch, "E89.right", {"start": v(25, 32.29) * mm, "end": v(25, 29.29) * mm});
            skLineSegment(sketch, "E90.bottom", {"start": v(-25, 20.29) * mm, "end": v(25, 20.29) * mm});
            skLineSegment(sketch, "E90.top", {"start": v(-25, 17.29) * mm, "end": v(25, 17.29) * mm});
            skLineSegment(sketch, "E90.left", {"start": v(-25, 20.29) * mm, "end": v(-25, 17.29) * mm});
            skLineSegment(sketch, "E90.right", {"start": v(25, 20.29) * mm, "end": v(25, 17.29) * mm});
            skLineSegment(sketch, "E91.bottom", {"start": v(25, 20.29) * mm, "end": v(19, 20.29) * mm});
            skLineSegment(sketch, "E91.top", {"start": v(25, 29.29) * mm, "end": v(19, 29.29) * mm});
            skLineSegment(sketch, "E91.left", {"start": v(25, 20.29) * mm, "end": v(25, 29.29) * mm});
            skLineSegment(sketch, "E91.right", {"start": v(19, 20.29) * mm, "end": v(19, 29.29) * mm});
            skLineSegment(sketch, "E92.bottom", {"start": v(-25, 20.29) * mm, "end": v(-19, 20.29) * mm});
            skLineSegment(sketch, "E92.top", {"start": v(-25, 29.29) * mm, "end": v(-19, 29.29) * mm});
            skLineSegment(sketch, "E92.left", {"start": v(-25, 20.29) * mm, "end": v(-25, 29.29) * mm});
            skLineSegment(sketch, "E92.right", {"start": v(-19, 20.29) * mm, "end": v(-19, 29.29) * mm});
            skPoint(sketch, "E93", {"position": v(0, 32.29) * mm});
            skSolve(sketch);
        }
        {
            var Q0;
            Q0 = qSketchRegion(id + "F12", true);
            extrude(context, id + "F13", {"entities" : qUnion([Q0]), "depth" : 3 * mm, "offsetDistance" : 25 * mm});
        }
        {
            var Q0;
            Q0=qCreatedBy(makeId("Front.planeOp"),FACE);
            var sketch = newSketch(context, id + "F14", { "sketchPlane" : qUnion([Q0])});
            skCircle(sketch, "E94", {"center": v(115.7, 57.44) * mm, "radius": 36 * mm});
            skLineSegment(sketch, "E95.bottom", {"start": v(120.2, 58.94) * mm, "end": v(111.2, 58.94) * mm});
            skLineSegment(sketch, "E95.top", {"start": v(120.2, 55.94) * mm, "end": v(111.2, 55.94) * mm});
            skLineSegment(sketch, "E95.left", {"start": v(120.2, 58.94) * mm, "end": v(120.2, 55.94) * mm});
            skLineSegment(sketch, "E95.right", {"start": v(111.2, 58.94) * mm, "end": v(111.2, 55.94) * mm});
            skLineSegment(sketch, "E96.bottom", {"start": v(117.2, 61.94) * mm, "end": v(114.2, 61.94) * mm});
            skLineSegment(sketch, "E96.top", {"start": v(117.2, 52.94) * mm, "end": v(114.2, 52.94) * mm});
            skLineSegment(sketch, "E96.left", {"start": v(117.2, 61.94) * mm, "end": v(117.2, 52.94) * mm});
            skLineSegment(sketch, "E96.right", {"start": v(114.2, 61.94) * mm, "end": v(114.2, 52.94) * mm});
            skSolve(sketch);
        }
        {
            var Q0;
            Q0=makeQuery(id+"F14.imprint","IMPRINT",FACE,{"disambiguationData":[TD([[makeQuery(id+"F14.imprint","IMPRINT",EDGE,{"derivedFrom":sQuery(id+"F14.wireOp",EDGE,"E94")}),1.0]])]});
            extrude(context, id + "F15", {"entities" : qUnion([Q0]), "depth" : 3 * mm, "offsetDistance" : 25 * mm});
        }
        {
            var Q0;
            Q0=makeQuery(id+"F13.opExtrude","CAP_FACE",FACE,{"disambiguationData":[OSD([sQuery(id+"F12.wireOp",EDGE,"E88.top"),sQuery(id+"F12.wireOp",EDGE,"E88.left"),sQuery(id+"F12.wireOp",EDGE,"E88.right"),sQuery(id+"F12.wireOp",EDGE,"E89.bottom"),sQuery(id+"F12.wireOp",EDGE,"E89.top"),sQuery(id+"F12.wireOp",EDGE,"E89.left"),sQuery(id+"F12.wireOp",EDGE,"E89.right"),sQuery(id+"F12.wireOp",EDGE,"E90.bottom"),sQuery(id+"F12.wireOp",EDGE,"E90.top"),sQuery(id+"F12.wireOp",EDGE,"E90.left"),sQuery(id+"F12.wireOp",EDGE,"E90.right"),sQuery(id+"F12.wireOp",EDGE,"E91.left"),sQuery(id+"F12.wireOp",EDGE,"E91.right"),sQuery(id+"F12.wireOp",EDGE,"E92.left"),sQuery(id+"F12.wireOp",EDGE,"E92.right")])],"isStart":false});
            var sketch = newSketch(context, id + "F16", { "sketchPlane" : qUnion([Q0])});
            skLineSegment(sketch, "E97", {"start": v(-25, 27.29) * mm, "end": v(-19, 27.29) * mm, "construction": true});
            skLineSegment(sketch, "E98", {"start": v(-25, 23.29) * mm, "end": v(-19, 23.29) * mm, "construction": true});
            skLineSegment(sketch, "E99.bottom", {"start": v(-19.1, 25.23) * mm, "end": v(-21.15, 27.29) * mm});
            skLineSegment(sketch, "E99.top", {"start": v(-21.15, 23.18) * mm, "end": v(-23.2, 25.23) * mm});
            skLineSegment(sketch, "E99.left", {"start": v(-19.1, 25.23) * mm, "end": v(-21.15, 23.18) * mm});
            skLineSegment(sketch, "E99.right", {"start": v(-21.15, 27.29) * mm, "end": v(-23.2, 25.23) * mm});
            skPoint(sketch, "E99.middle", {"position": v(-21.15, 25.23) * mm});
            skLineSegment(sketch, "E100.MirrorCS", {"start": v(19.1, 25.23) * mm, "end": v(21.15, 27.29) * mm});
            skPoint(sketch, "E101.MirrorP", {"position": v(21.15, 25.23) * mm});
            skLineSegment(sketch, "E102.MirrorCS", {"start": v(25, 27.29) * mm, "end": v(19, 27.29) * mm, "construction": true});
            skLineSegment(sketch, "E103.MirrorCS", {"start": v(25, 23.29) * mm, "end": v(19, 23.29) * mm, "construction": true});
            skLineSegment(sketch, "E104.MirrorCS", {"start": v(21.15, 27.29) * mm, "end": v(23.2, 25.23) * mm});
            skLineSegment(sketch, "E105.MirrorCS", {"start": v(19.1, 25.23) * mm, "end": v(21.15, 23.18) * mm});
            skLineSegment(sketch, "E106.MirrorCS", {"start": v(21.15, 23.18) * mm, "end": v(23.2, 25.23) * mm});
            skSolve(sketch);
        }
        {
            var Q0;
            Q0=makeQuery(id+"F16.imprint","IMPRINT",FACE,{"disambiguationData":[TD([[makeQuery(id+"F16.imprint","IMPRINT",EDGE,{"derivedFrom":sQuery(id+"F16.wireOp",EDGE,"E99.bottom")}),1.0]])]});
            var Q1;
            Q1=makeQuery(id+"F16.imprint","IMPRINT",FACE,{"disambiguationData":[TD([[makeQuery(id+"F16.imprint","IMPRINT",EDGE,{"derivedFrom":sQuery(id+"F16.wireOp",EDGE,"E105.MirrorCS")}),1.0]])]});
            var Q2;
            Q2=makeQuery(id+"F13.opExtrude","CAP_FACE",FACE,{"disambiguationData":[OSD([sQuery(id+"F12.wireOp",EDGE,"E88.top"),sQuery(id+"F12.wireOp",EDGE,"E88.left"),sQuery(id+"F12.wireOp",EDGE,"E88.right"),sQuery(id+"F12.wireOp",EDGE,"E89.bottom"),sQuery(id+"F12.wireOp",EDGE,"E89.top"),sQuery(id+"F12.wireOp",EDGE,"E89.left"),sQuery(id+"F12.wireOp",EDGE,"E89.right"),sQuery(id+"F12.wireOp",EDGE,"E90.bottom"),sQuery(id+"F12.wireOp",EDGE,"E90.top"),sQuery(id+"F12.wireOp",EDGE,"E90.left"),sQuery(id+"F12.wireOp",EDGE,"E90.right"),sQuery(id+"F12.wireOp",EDGE,"E91.left"),sQuery(id+"F12.wireOp",EDGE,"E91.right"),sQuery(id+"F12.wireOp",EDGE,"E92.left"),sQuery(id+"F12.wireOp",EDGE,"E92.right")])],"isStart":true});
            extrude(context, id + "F17", {"entities" : qUnion([Q0, Q1]), "operationType" : NewBodyOperationType.REMOVE, "endBound" : BoundingType.UP_TO_SURFACE, "oppositeDirection" : true, "depth" : 25 * mm, "endBoundEntityFace" : qUnion([Q2]), "offsetDistance" : 25 * mm});
        }
        {
            var Q0;
            Q0=makeQuery(id+"F7.opExtrude","CAP_FACE",FACE,{"disambiguationData":[OSD([sQuery(id+"F6.wireOp",EDGE,"E56.bottom"),sQuery(id+"F6.wireOp",EDGE,"E56.top"),sQuery(id+"F6.wireOp",EDGE,"E56.left"),sQuery(id+"F6.wireOp",EDGE,"E56.right"),sQuery(id+"F6.wireOp",EDGE,"E57.top"),sQuery(id+"F6.wireOp",EDGE,"E57.left"),sQuery(id+"F6.wireOp",EDGE,"E57.right"),sQuery(id+"F6.wireOp",EDGE,"E58.top"),sQuery(id+"F6.wireOp",EDGE,"E58.left"),sQuery(id+"F6.wireOp",EDGE,"E58.right"),sQuery(id+"F6.wireOp",EDGE,"E59.bottom"),sQuery(id+"F6.wireOp",EDGE,"E59.top"),sQuery(id+"F6.wireOp",EDGE,"E59.right"),sQuery(id+"F6.wireOp",EDGE,"E60.bottom"),sQuery(id+"F6.wireOp",EDGE,"E60.top"),sQuery(id+"F6.wireOp",EDGE,"E60.right"),sQuery(id+"F6.wireOp",EDGE,"E61")])],"isStart":false});
            var sketch = newSketch(context, id + "F18", { "sketchPlane" : qUnion([Q0])});
            skLineSegment(sketch, "E107.bottom", {"start": v(21, 4.5) * mm, "end": v(18, 4.5) * mm});
            skLineSegment(sketch, "E107.top", {"start": v(21, -4.5) * mm, "end": v(18, -4.5) * mm});
            skLineSegment(sketch, "E107.left", {"start": v(21, 4.5) * mm, "end": v(21, -4.5) * mm});
            skLineSegment(sketch, "E107.right", {"start": v(18, 4.5) * mm, "end": v(18, -4.5) * mm});
            skPoint(sketch, "E107.middle", {"position": v(19.5, 0) * mm});
            skLineSegment(sketch, "E108.bottom", {"start": v(4.5, -18) * mm, "end": v(-4.5, -18) * mm});
            skLineSegment(sketch, "E108.top", {"start": v(4.5, -21) * mm, "end": v(-4.5, -21) * mm});
            skLineSegment(sketch, "E108.left", {"start": v(4.5, -18) * mm, "end": v(4.5, -21) * mm});
            skLineSegment(sketch, "E108.right", {"start": v(-4.5, -18) * mm, "end": v(-4.5, -21) * mm});
            skPoint(sketch, "E108.middle", {"position": v(0, -19.5) * mm});
            skSolve(sketch);
        }
        {
            var Q0;
            Q0=makeQuery(id+"F18.imprint","IMPRINT",FACE,{"disambiguationData":[TD([[makeQuery(id+"F18.imprint","IMPRINT",EDGE,{"derivedFrom":sQuery(id+"F18.wireOp",EDGE,"E107.bottom")}),1.0]])]});
            var Q1;
            Q1=makeQuery(id+"F18.imprint","IMPRINT",FACE,{"disambiguationData":[TD([[makeQuery(id+"F18.imprint","IMPRINT",EDGE,{"derivedFrom":sQuery(id+"F18.wireOp",EDGE,"E108.bottom")}),1.0]])]});
            var Q2;
            Q2=makeQuery(id+"F1.opExtrude","CAP_FACE",FACE,{"disambiguationData":[OSD([sQuery(id+"F0.wireOp",EDGE,"E0.bottom"),sQuery(id+"F0.wireOp",EDGE,"E0.top"),sQuery(id+"F0.wireOp",EDGE,"E0.left"),sQuery(id+"F0.wireOp",EDGE,"E0.right"),sQuery(id+"F0.wireOp",EDGE,"E1.top"),sQuery(id+"F0.wireOp",EDGE,"E1.left"),sQuery(id+"F0.wireOp",EDGE,"E1.right"),sQuery(id+"F0.wireOp",EDGE,"E2.bottom"),sQuery(id+"F0.wireOp",EDGE,"E2.top"),sQuery(id+"F0.wireOp",EDGE,"E2.right"),sQuery(id+"F0.wireOp",EDGE,"E3.top"),sQuery(id+"F0.wireOp",EDGE,"E3.left"),sQuery(id+"F0.wireOp",EDGE,"E3.right"),sQuery(id+"F0.wireOp",EDGE,"E4.bottom"),sQuery(id+"F0.wireOp",EDGE,"E4.top"),sQuery(id+"F0.wireOp",EDGE,"E4.right"),sQuery(id+"F0.wireOp",EDGE,"E9"),sQuery(id+"F0.wireOp",EDGE,"E10.bottom"),sQuery(id+"F0.wireOp",EDGE,"E10.top"),sQuery(id+"F0.wireOp",EDGE,"E10.left"),sQuery(id+"F0.wireOp",EDGE,"E10.right"),sQuery(id+"F0.wireOp",EDGE,"E11.bottom"),sQuery(id+"F0.wireOp",EDGE,"E11.top"),sQuery(id+"F0.wireOp",EDGE,"E11.left"),sQuery(id+"F0.wireOp",EDGE,"E11.right")])],"isStart":true});
            extrude(context, id + "F19", {"entities" : qUnion([Q0, Q1]), "operationType" : NewBodyOperationType.REMOVE, "endBound" : BoundingType.UP_TO_SURFACE, "oppositeDirection" : true, "depth" : 25 * mm, "endBoundEntityFace" : qUnion([Q2]), "offsetDistance" : 25 * mm});
        }
        {
            var Q0;
            {var subQ0=sQuery(id+"F0.wireOp",EDGE,"E11.right");var subQ1=sQuery(id+"F0.wireOp",EDGE,"E11.left");var subQ2=sQuery(id+"F0.wireOp",EDGE,"E11.top");var subQ3=sQuery(id+"F0.wireOp",EDGE,"E11.bottom");var subQ4=sQuery(id+"F0.wireOp",EDGE,"E10.right");var subQ5=sQuery(id+"F0.wireOp",EDGE,"E10.left");var subQ6=sQuery(id+"F0.wireOp",EDGE,"E10.top");var subQ7=sQuery(id+"F0.wireOp",EDGE,"E10.bottom");var subQ8=sQuery(id+"F0.wireOp",EDGE,"E9");var subQ9=sQuery(id+"F0.wireOp",EDGE,"E4.right");var subQ10=sQuery(id+"F0.wireOp",EDGE,"E4.top");var subQ11=sQuery(id+"F0.wireOp",EDGE,"E4.bottom");var subQ12=sQuery(id+"F0.wireOp",EDGE,"E3.right");var subQ13=sQuery(id+"F0.wireOp",EDGE,"E3.left");var subQ14=sQuery(id+"F0.wireOp",EDGE,"E3.top");var subQ15=sQuery(id+"F0.wireOp",EDGE,"E2.right");var subQ16=sQuery(id+"F0.wireOp",EDGE,"E2.top");var subQ17=sQuery(id+"F0.wireOp",EDGE,"E2.bottom");var subQ18=sQuery(id+"F0.wireOp",EDGE,"E1.right");var subQ19=sQuery(id+"F0.wireOp",EDGE,"E1.left");var subQ20=sQuery(id+"F0.wireOp",EDGE,"E1.top");var subQ21=sQuery(id+"F0.wireOp",EDGE,"E0.right");var subQ22=sQuery(id+"F0.wireOp",EDGE,"E0.left");var subQ23=sQuery(id+"F0.wireOp",EDGE,"E0.top");var subQ24=sQuery(id+"F0.wireOp",EDGE,"E0.bottom");Q0=makeQuery(id+"F19.boolean.opBoolean","COPY",FACE,{"disambiguationData":[TD([makeQuery(id+"F1.opExtrude","CAP_FACE",FACE,{"disambiguationData":[OSD([subQ24,subQ23,subQ22,subQ21,subQ20,subQ19,subQ18,subQ17,subQ16,subQ15,subQ14,subQ13,subQ12,subQ11,subQ10,subQ9,subQ8,subQ7,subQ6,subQ5,subQ4,subQ3,subQ2,subQ1,subQ0])],"isStart":true})])],"derivedFrom":makeQuery(id+"F19.opExtrude","SWEPT_FACE",FACE,{"disambiguationData":[OSD([sQuery(id+"F18.wireOp",EDGE,"E107.left")])]})});}
            var sketch = newSketch(context, id + "F20", { "sketchPlane" : qUnion([Q0])});
            skLineSegment(sketch, "E109.bottom", {"start": v(-7.5, 3) * mm, "end": v(7.5, 3) * mm});
            skLineSegment(sketch, "E109.top", {"start": v(-7.5, 34) * mm, "end": v(7.5, 34) * mm});
            skLineSegment(sketch, "E109.left", {"start": v(-7.5, 3) * mm, "end": v(-7.5, 34) * mm});
            skLineSegment(sketch, "E109.right", {"start": v(7.5, 3) * mm, "end": v(7.5, 34) * mm});
            skLineSegment(sketch, "E110.bottom", {"start": v(4.5, 3) * mm, "end": v(-4.5, 3) * mm});
            skLineSegment(sketch, "E110.top", {"start": v(4.5, 0) * mm, "end": v(-4.5, 0) * mm});
            skLineSegment(sketch, "E110.left", {"start": v(4.5, 3) * mm, "end": v(4.5, 0) * mm});
            skLineSegment(sketch, "E110.right", {"start": v(-4.5, 3) * mm, "end": v(-4.5, 0) * mm});
            skLineSegment(sketch, "E111.bottom", {"start": v(-4.5, 34) * mm, "end": v(4.5, 34) * mm});
            skLineSegment(sketch, "E111.top", {"start": v(-4.5, 37) * mm, "end": v(4.5, 37) * mm});
            skLineSegment(sketch, "E111.left", {"start": v(-4.5, 34) * mm, "end": v(-4.5, 37) * mm});
            skLineSegment(sketch, "E111.right", {"start": v(4.5, 34) * mm, "end": v(4.5, 37) * mm});
            skPoint(sketch, "E112", {"position": v(0, 34) * mm});
            skCircle(sketch, "E113.0", {"center": v(0, 20) * mm, "radius": 2.3 * mm});
            skSolve(sketch);
        }
        {
            var Q0;
            Q0 = qSketchRegion(id + "F20", true);
            extrude(context, id + "F21", {"entities" : qUnion([Q0]), "depth" : 3 * mm, "offsetDistance" : 25 * mm});
        }
    });
